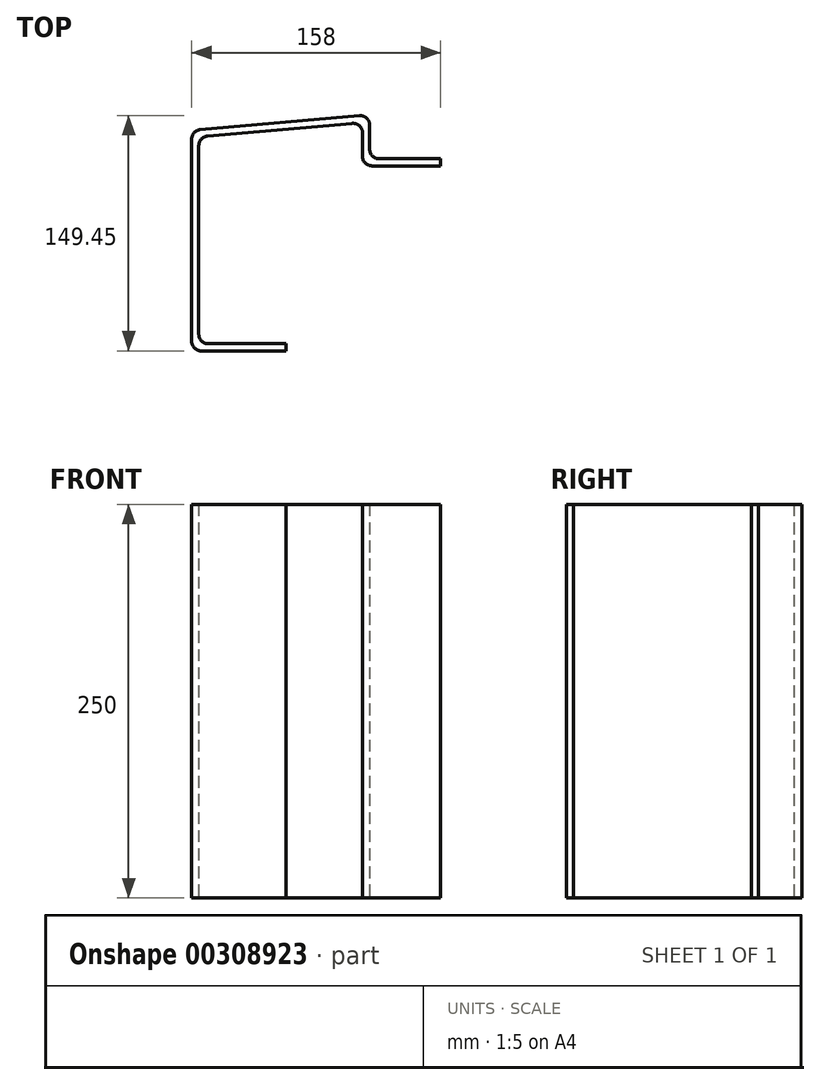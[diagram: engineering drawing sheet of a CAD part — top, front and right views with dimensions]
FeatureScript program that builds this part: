
annotation { "Feature Type Name" : "Feature", "Feature Type Description" : "" }
export const myFeature = defineFeature(function(context is Context, id is Id, definition is map)
    precondition{}
    {
        {
            var Q0;
            Q0=qCreatedBy(makeId("Top.planeOp"),FACE);
            var sketch = newSketch(context, id + "F0", { "sketchPlane" : qUnion([Q0])});
            skLineSegment(sketch, "E0", {"start": v(0, 0) * mm, "end": v(-54, 0) * mm});
            skLineSegment(sketch, "E1", {"start": v(-60, 0) * mm, "end": v(-60, 150) * mm, "construction": true});
            skLineSegment(sketch, "E2", {"start": v(-60, 150) * mm, "end": v(53, 150) * mm, "construction": true});
            skLineSegment(sketch, "E3", {"start": v(46.47, 149.42) * mm, "end": v(-54.53, 140.48) * mm});
            skLineSegment(sketch, "E4", {"start": v(53, 143.45) * mm, "end": v(53, 128) * mm});
            skLineSegment(sketch, "E5", {"start": v(59, 122) * mm, "end": v(98, 122) * mm});
            skLineSegment(sketch, "E6", {"start": v(-60, 134.5) * mm, "end": v(-60, 6) * mm});
            skLineSegment(sketch, "E7.0", {"start": v(54.5, 117.5) * mm, "end": v(98, 117.5) * mm});
            skLineSegment(sketch, "E7.1", {"start": v(0, 4.5) * mm, "end": v(-49.5, 4.5) * mm});
            skLineSegment(sketch, "E7.2", {"start": v(-55.5, 130.39) * mm, "end": v(-55.5, 10.5) * mm});
            skLineSegment(sketch, "E7.3", {"start": v(41.97, 144.5) * mm, "end": v(-50.03, 136.36) * mm});
            skLineSegment(sketch, "E7.4", {"start": v(48.5, 138.53) * mm, "end": v(48.5, 123.5) * mm});
            skLineSegment(sketch, "E8", {"start": v(0, 0) * mm, "end": v(0, 4.5) * mm});
            skLineSegment(sketch, "E9", {"start": v(98, 122) * mm, "end": v(98, 117.5) * mm});
            skPoint(sketch, "E10.visualSharp", {"position": v(-55.5, 4.5) * mm});
            skArc(sketch, "E10.filletArc", {"start": v(-55.5, 10.5) * mm, "mid": v(-53.74, 6.26) * mm, "end": v(-49.5, 4.5) * mm});
            skPoint(sketch, "E11.visualSharp", {"position": v(-60, 0) * mm});
            skArc(sketch, "E11.filletArc", {"start": v(-60, 6) * mm, "mid": v(-58.24, 1.76) * mm, "end": v(-54, 0) * mm});
            skPoint(sketch, "E12.visualSharp", {"position": v(-60, 140) * mm});
            skArc(sketch, "E12.filletArc", {"start": v(-54.53, 140.48) * mm, "mid": v(-58.43, 138.56) * mm, "end": v(-60, 134.5) * mm});
            skPoint(sketch, "E13.visualSharp", {"position": v(-55.5, 135.88) * mm});
            skArc(sketch, "E13.filletArc", {"start": v(-50.03, 136.36) * mm, "mid": v(-53.93, 134.44) * mm, "end": v(-55.5, 130.39) * mm});
            skPoint(sketch, "E14.visualSharp", {"position": v(48.5, 145.08) * mm});
            skArc(sketch, "E14.filletArc", {"start": v(48.5, 138.53) * mm, "mid": v(46.55, 142.96) * mm, "end": v(41.97, 144.5) * mm});
            skPoint(sketch, "E15.visualSharp", {"position": v(53, 150) * mm});
            skArc(sketch, "E15.filletArc", {"start": v(53, 143.45) * mm, "mid": v(51.05, 147.87) * mm, "end": v(46.47, 149.42) * mm});
            skPoint(sketch, "E16.visualSharp", {"position": v(53, 122) * mm});
            skArc(sketch, "E16.filletArc", {"start": v(53, 128) * mm, "mid": v(54.76, 123.76) * mm, "end": v(59, 122) * mm});
            skPoint(sketch, "E17.visualSharp", {"position": v(48.5, 117.5) * mm});
            skArc(sketch, "E17.filletArc", {"start": v(48.5, 123.5) * mm, "mid": v(50.26, 119.26) * mm, "end": v(54.5, 117.5) * mm});
            skSolve(sketch);
        }
        {
            var Q0;
            Q0 = qSketchRegion(id + "F0", true);
            extrude(context, id + "F1", {"entities" : qUnion([Q0]), "depth" : 250 * mm});
        }
    });
